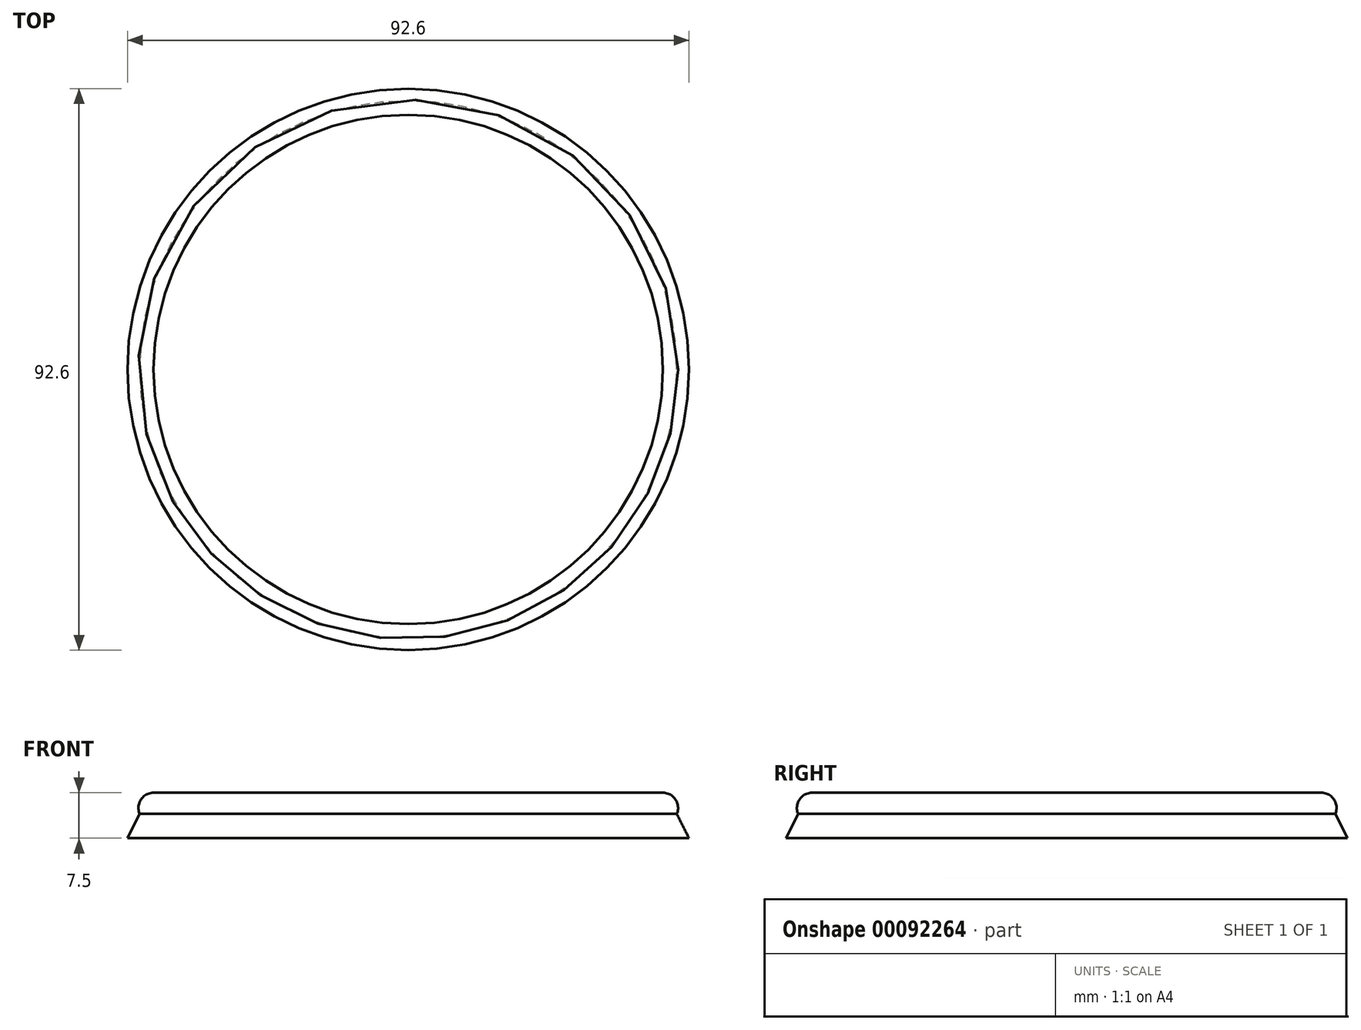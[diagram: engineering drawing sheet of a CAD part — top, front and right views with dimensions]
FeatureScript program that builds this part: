
annotation { "Feature Type Name" : "Feature", "Feature Type Description" : "" }
export const myFeature = defineFeature(function(context is Context, id is Id, definition is map)
    precondition{}
    {
        {
            var Q0;
            Q0=qCreatedBy(makeId("Front.planeOp"),FACE);
            var sketch = newSketch(context, id + "F0", { "sketchPlane" : qUnion([Q0])});
            skLineSegment(sketch, "E0", {"start": v(0, 0) * mm, "end": v(0, 7.5) * mm, "construction": true});
            skLineSegment(sketch, "E1", {"start": v(0, 7.5) * mm, "end": v(42, 7.5) * mm, "construction": true});
            skArc(sketch, "E2", {"start": v(42, 7.5) * mm, "mid": v(44.1, 6.37) * mm, "end": v(44.3, 4) * mm});
            skLineSegment(sketch, "E3", {"start": v(44.3, 4) * mm, "end": v(46.3, 0) * mm});
            skSolve(sketch);
        }
        {
            var Q0;
            Q0 = qConstructionFilter(qBodyType(qCreatedBy(id + "F0" ,EDGE), BodyType.WIRE), ConstructionObject.NO);
            var Q1;
            Q1=sQuery(id+"F0.wireOp",EDGE,"E0");
            revolve(context, id + "F1", {"bodyType" : ToolBodyType.SURFACE, "surfaceEntities" : qUnion([Q0]), "axis" : qUnion([Q1]), "revolveType" : RevolveType.FULL});
        }
    });
